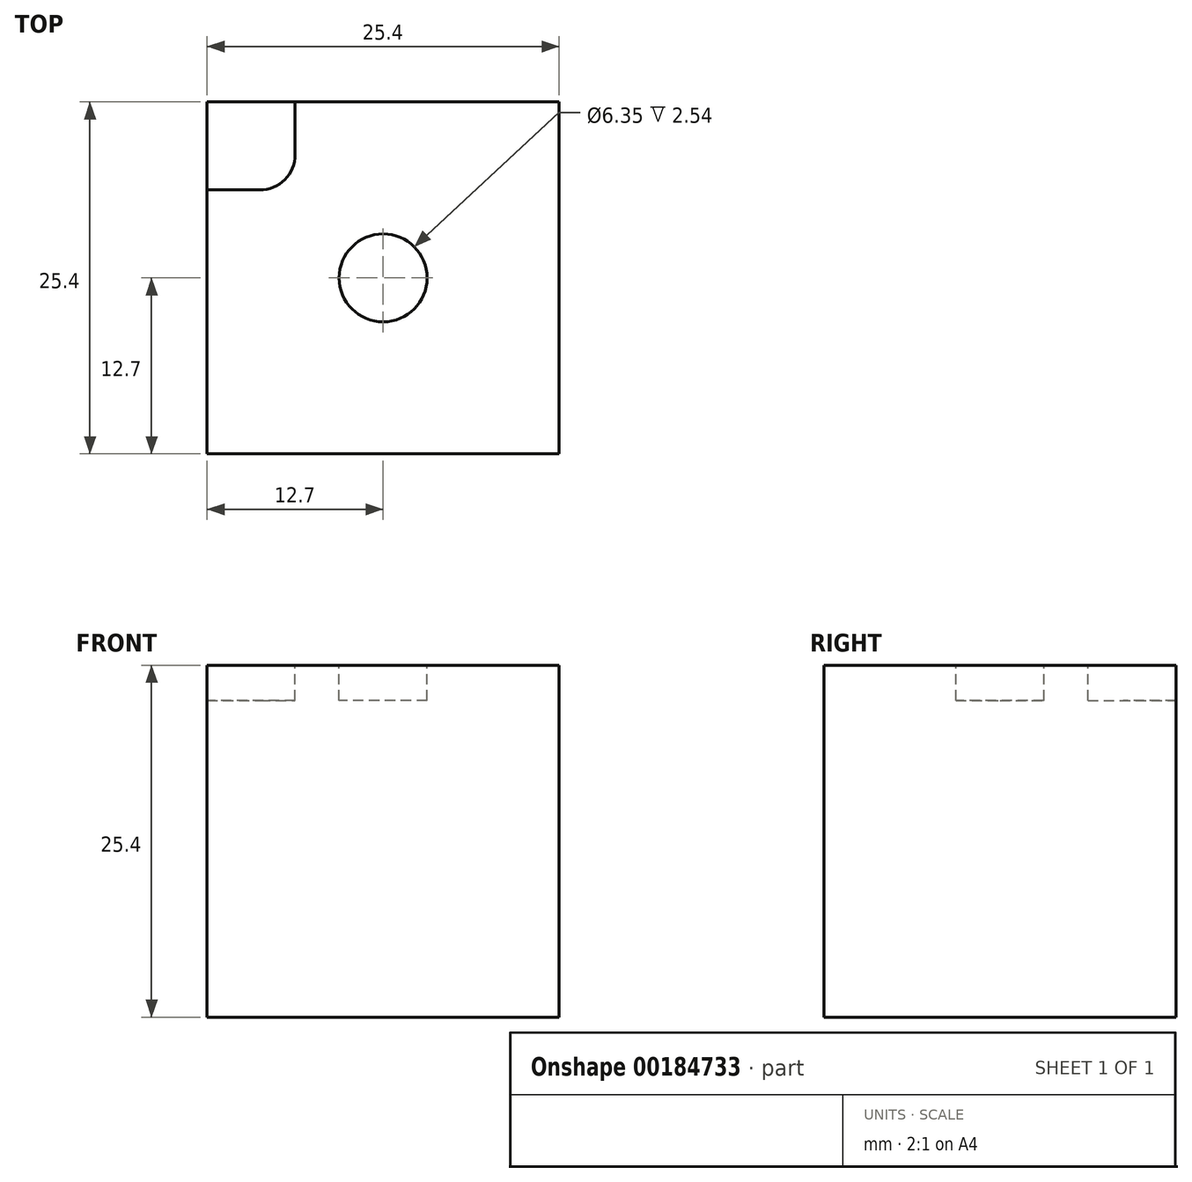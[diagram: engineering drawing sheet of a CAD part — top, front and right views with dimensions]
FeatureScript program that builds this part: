
annotation { "Feature Type Name" : "Feature", "Feature Type Description" : "" }
export const myFeature = defineFeature(function(context is Context, id is Id, definition is map)
    precondition{}
    {
        {
            var Q0;
            Q0=qCreatedBy(makeId("Top.planeOp"),FACE);
            var sketch = newSketch(context, id + "F0", { "sketchPlane" : qUnion([Q0])});
            skLineSegment(sketch, "E0.bottom", {"start": v(12.7, -12.7) * mm, "end": v(-12.7, -12.7) * mm});
            skLineSegment(sketch, "E0.top", {"start": v(12.7, 12.7) * mm, "end": v(-12.7, 12.7) * mm});
            skLineSegment(sketch, "E0.left", {"start": v(12.7, -12.7) * mm, "end": v(12.7, 12.7) * mm});
            skLineSegment(sketch, "E0.right", {"start": v(-12.7, -12.7) * mm, "end": v(-12.7, 12.7) * mm});
            skPoint(sketch, "E0.middle", {"position": v(0, 0) * mm});
            skSolve(sketch);
        }
        {
            var Q0;
            Q0 = qSketchRegion(id + "F0", true);
            extrude(context, id + "F1", {"entities" : qUnion([Q0]), "depth" : 25.4 * mm});
        }
        {
            var Q0;
            Q0=makeQuery(id+"F1.opExtrude","CAP_FACE",FACE,{"disambiguationData":[OSD([sQuery(id+"F0.wireOp",EDGE,"E0.bottom"),sQuery(id+"F0.wireOp",EDGE,"E0.top"),sQuery(id+"F0.wireOp",EDGE,"E0.left"),sQuery(id+"F0.wireOp",EDGE,"E0.right")])],"isStart":false});
            var sketch = newSketch(context, id + "F2", { "sketchPlane" : qUnion([Q0])});
            skLineSegment(sketch, "E1.bottom", {"start": v(-12.7, 12.7) * mm, "end": v(-6.35, 12.7) * mm});
            skLineSegment(sketch, "E1.top", {"start": v(-12.7, 6.35) * mm, "end": v(-6.35, 6.35) * mm});
            skLineSegment(sketch, "E1.left", {"start": v(-12.7, 12.7) * mm, "end": v(-12.7, 6.35) * mm});
            skLineSegment(sketch, "E1.right", {"start": v(-6.35, 12.7) * mm, "end": v(-6.35, 6.35) * mm});
            skCircle(sketch, "E2", {"center": v(0, 0) * mm, "radius": 3.18 * mm});
            skSolve(sketch);
        }
        {
            var Q0;
            Q0=makeQuery(id+"F2.imprint","IMPRINT",FACE,{"disambiguationData":[TD([[makeQuery(id+"F2.imprint","IMPRINT",EDGE,{"derivedFrom":sQuery(id+"F2.wireOp",EDGE,"E1.bottom")}),1.0]])]});
            var Q1;
            Q1=makeQuery(id+"F2.imprint","IMPRINT",FACE,{"disambiguationData":[TD([[makeQuery(id+"F2.imprint","IMPRINT",EDGE,{"derivedFrom":sQuery(id+"F2.wireOp",EDGE,"E2")}),1.0]])]});
            extrude(context, id + "F3", {"entities" : qUnion([Q0, Q1]), "operationType" : NewBodyOperationType.REMOVE, "oppositeDirection" : true, "depth" : 2.54 * mm});
        }
        {
            var Q0;
            Q0=makeQuery(id+"F3.boolean.opBoolean","COPY",EDGE,{"derivedFrom":makeQuery(id+"F3.opExtrude","SWEPT_EDGE",EDGE,{"disambiguationData":[OSD([sQuery(id+"F2.wireOp",EDGE,"E1.top"),sQuery(id+"F2.wireOp",EDGE,"E1.right")])]})});
            fillet(context, id + "F4", {"entities" : qUnion([Q0]), "radius" : 2.54 * mm, "tangentPropagation" : true, "allowEdgeOverflow" : false});
        }
    });
